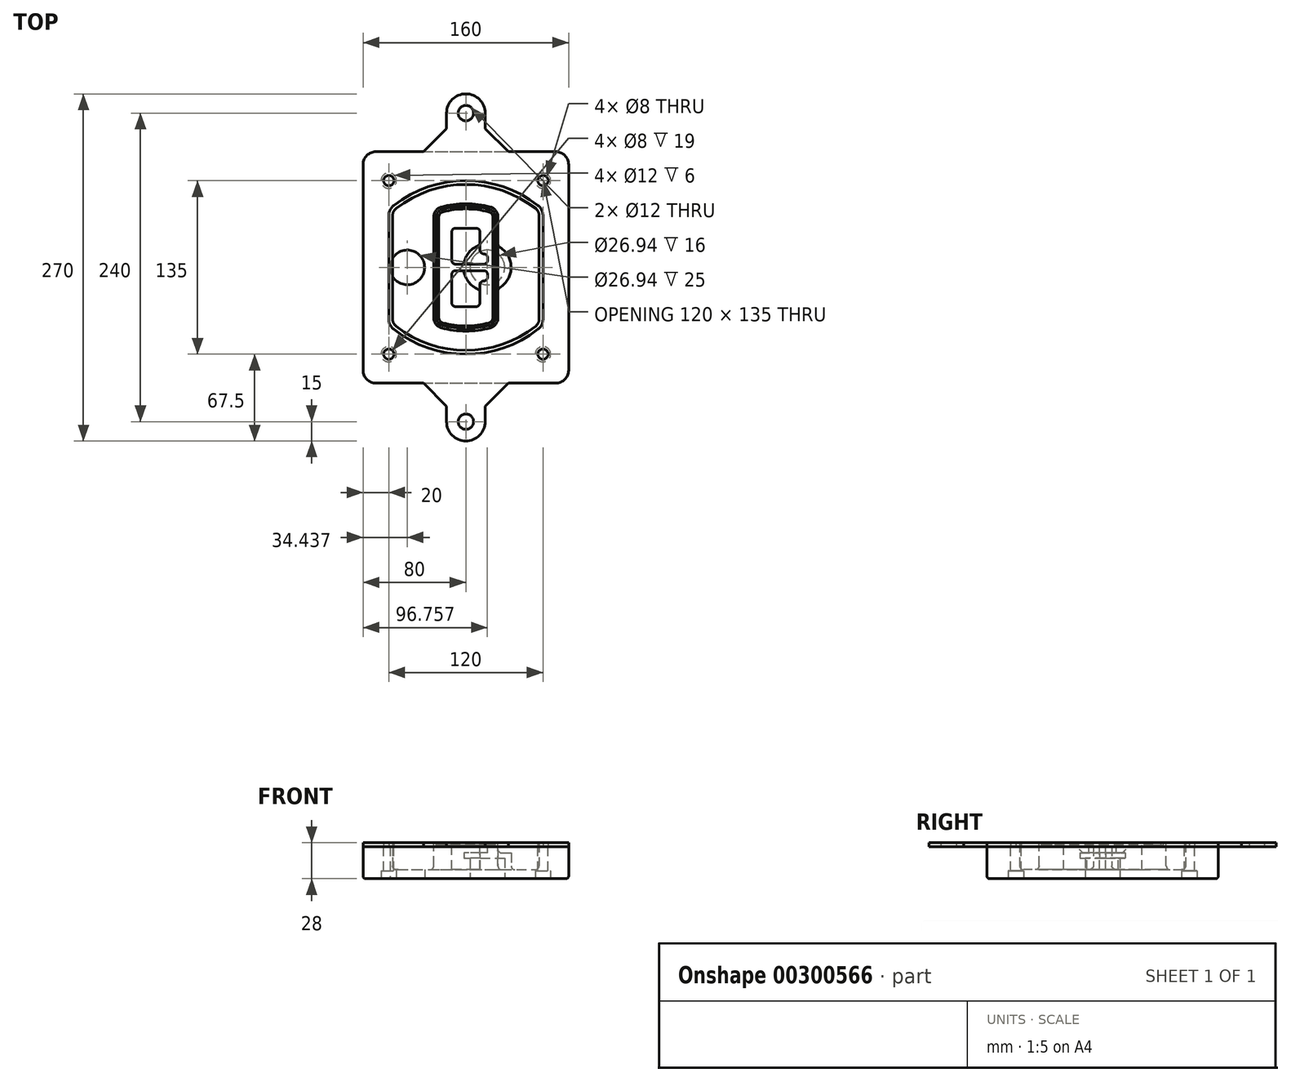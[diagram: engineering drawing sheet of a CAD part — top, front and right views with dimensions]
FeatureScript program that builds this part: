
annotation { "Feature Type Name" : "Feature", "Feature Type Description" : "" }
export const myFeature = defineFeature(function(context is Context, id is Id, definition is map)
    precondition{}
    {
        {
            var Q0;
            Q0=qCreatedBy(makeId("Top.planeOp"),FACE);
            var sketch = newSketch(context, id + "F0", { "sketchPlane" : qUnion([Q0])});
            skPoint(sketch, "E0.rect.middle", {"position": v(0, 0) * mm});
            skLineSegment(sketch, "E1.bottom", {"start": v(-70, -90) * mm, "end": v(70, -90) * mm});
            skLineSegment(sketch, "E1.top", {"start": v(-70, 90) * mm, "end": v(70, 90) * mm});
            skLineSegment(sketch, "E1.left", {"start": v(-80, -80) * mm, "end": v(-80, 80) * mm});
            skLineSegment(sketch, "E1.right", {"start": v(80, -80) * mm, "end": v(80, 80) * mm});
            skLineSegment(sketch, "E2", {"start": v(-80, 90) * mm, "end": v(80, -90) * mm, "construction": true});
            skLineSegment(sketch, "E3", {"start": v(80, 90) * mm, "end": v(-80, -90) * mm, "construction": true});
            skCircle(sketch, "E4", {"center": v(-60, 67.5) * mm, "radius": 4 * mm});
            skCircle(sketch, "E5", {"center": v(60, 67.5) * mm, "radius": 4 * mm});
            skCircle(sketch, "E6", {"center": v(60, -67.5) * mm, "radius": 4 * mm});
            skCircle(sketch, "E7", {"center": v(-60, -67.5) * mm, "radius": 4 * mm});
            skLineSegment(sketch, "E8", {"start": v(-60, 67.5) * mm, "end": v(60, 67.5) * mm, "construction": true});
            skLineSegment(sketch, "E9", {"start": v(60, 67.5) * mm, "end": v(60, -67.5) * mm, "construction": true});
            skLineSegment(sketch, "E10", {"start": v(60, -67.5) * mm, "end": v(-60, -67.5) * mm, "construction": true});
            skLineSegment(sketch, "E11", {"start": v(-60, -67.5) * mm, "end": v(-60, 67.5) * mm, "construction": true});
            skLineSegment(sketch, "E12", {"start": v(-60, 40.3) * mm, "end": v(-60, -40.3) * mm});
            skLineSegment(sketch, "E13", {"start": v(60, 40.3) * mm, "end": v(60, -40.3) * mm});
            skArc(sketch, "E14", {"start": v(56.15, 48.18) * mm, "mid": v(0, 67.5) * mm, "end": v(-56.15, 48.18) * mm});
            skArc(sketch, "E15", {"start": v(-56.15, -48.18) * mm, "mid": v(0, -67.5) * mm, "end": v(56.15, -48.18) * mm});
            skLineSegment(sketch, "E16", {"start": v(-60, 0) * mm, "end": v(60, 0) * mm, "construction": true});
            skPoint(sketch, "E17.visualSharp", {"position": v(-60, -45) * mm});
            skArc(sketch, "E17.filletArc", {"start": v(-60, -40.3) * mm, "mid": v(-58.99, -44.68) * mm, "end": v(-56.15, -48.18) * mm});
            skPoint(sketch, "E18.visualSharp", {"position": v(-60, 45) * mm});
            skArc(sketch, "E18.filletArc", {"start": v(-56.15, 48.18) * mm, "mid": v(-58.99, 44.68) * mm, "end": v(-60, 40.3) * mm});
            skPoint(sketch, "E19.visualSharp", {"position": v(60, 45) * mm});
            skArc(sketch, "E19.filletArc", {"start": v(60, 40.3) * mm, "mid": v(58.99, 44.68) * mm, "end": v(56.15, 48.18) * mm});
            skPoint(sketch, "E20.visualSharp", {"position": v(60, -45) * mm});
            skArc(sketch, "E20.filletArc", {"start": v(56.15, -48.18) * mm, "mid": v(58.99, -44.68) * mm, "end": v(60, -40.3) * mm});
            skPoint(sketch, "E21.visualSharp", {"position": v(-80, 90) * mm});
            skArc(sketch, "E21.filletArc", {"start": v(-70, 90) * mm, "mid": v(-77.07, 87.07) * mm, "end": v(-80, 80) * mm});
            skPoint(sketch, "E22.visualSharp", {"position": v(80, 90) * mm});
            skArc(sketch, "E22.filletArc", {"start": v(80, 80) * mm, "mid": v(77.07, 87.07) * mm, "end": v(70, 90) * mm});
            skPoint(sketch, "E23.visualSharp", {"position": v(80, -90) * mm});
            skArc(sketch, "E23.filletArc", {"start": v(70, -90) * mm, "mid": v(77.07, -87.07) * mm, "end": v(80, -80) * mm});
            skPoint(sketch, "E24.visualSharp", {"position": v(-80, -90) * mm});
            skArc(sketch, "E24.filletArc", {"start": v(-80, -80) * mm, "mid": v(-77.07, -87.07) * mm, "end": v(-70, -90) * mm});
            skArc(sketch, "E25.0", {"start": v(57, 40.3) * mm, "mid": v(56.3, 43.36) * mm, "end": v(54.3, 45.81) * mm});
            skLineSegment(sketch, "E25.1", {"start": v(57, 40.3) * mm, "end": v(57, -40.3) * mm});
            skArc(sketch, "E25.2", {"start": v(54.3, -45.81) * mm, "mid": v(56.3, -43.36) * mm, "end": v(57, -40.3) * mm});
            skArc(sketch, "E25.3", {"start": v(-54.3, -45.81) * mm, "mid": v(0, -64.5) * mm, "end": v(54.3, -45.81) * mm});
            skArc(sketch, "E25.4", {"start": v(-57, -40.3) * mm, "mid": v(-56.3, -43.36) * mm, "end": v(-54.3, -45.81) * mm});
            skArc(sketch, "E25.5", {"start": v(54.3, 45.81) * mm, "mid": v(0, 64.5) * mm, "end": v(-54.3, 45.81) * mm});
            skLineSegment(sketch, "E25.6", {"start": v(-57, 40.3) * mm, "end": v(-57, -40.3) * mm});
            skArc(sketch, "E25.7", {"start": v(-54.3, 45.81) * mm, "mid": v(-56.3, 43.36) * mm, "end": v(-57, 40.3) * mm});
            skArc(sketch, "E26.0", {"start": v(-58.62, 51.33) * mm, "mid": v(-62.58, 46.43) * mm, "end": v(-64, 40.3) * mm});
            skArc(sketch, "E26.1", {"start": v(58.62, 51.33) * mm, "mid": v(0, 71.5) * mm, "end": v(-58.62, 51.33) * mm});
            skArc(sketch, "E26.2", {"start": v(64, 40.3) * mm, "mid": v(62.58, 46.43) * mm, "end": v(58.62, 51.33) * mm});
            skLineSegment(sketch, "E26.3", {"start": v(64, 40.3) * mm, "end": v(64, -40.3) * mm});
            skArc(sketch, "E26.4", {"start": v(58.62, -51.33) * mm, "mid": v(62.58, -46.43) * mm, "end": v(64, -40.3) * mm});
            skLineSegment(sketch, "E26.5", {"start": v(-64, 40.3) * mm, "end": v(-64, -40.3) * mm});
            skArc(sketch, "E26.6", {"start": v(-58.62, -51.33) * mm, "mid": v(0, -71.5) * mm, "end": v(58.62, -51.33) * mm});
            skArc(sketch, "E26.7", {"start": v(-64, -40.3) * mm, "mid": v(-62.58, -46.43) * mm, "end": v(-58.62, -51.33) * mm});
            skSolve(sketch);
        }
        {
            var Q0;
            Q0=makeQuery(id+"F0.imprint","IMPRINT",FACE,{"disambiguationData":[TD([[makeQuery(id+"F0.imprint","IMPRINT",EDGE,{"derivedFrom":sQuery(id+"F0.wireOp",EDGE,"E1.bottom")}),1.0]])]});
            var Q1;
            Q1=makeQuery(id+"F0.imprint","IMPRINT",FACE,{"disambiguationData":[TD([[makeQuery(id+"F0.imprint","IMPRINT",EDGE,{"derivedFrom":sQuery(id+"F0.wireOp",EDGE,"E12")}),1.0]])]});
            var Q2;
            Q2=makeQuery(id+"F0.imprint","IMPRINT",FACE,{"disambiguationData":[TD([[makeQuery(id+"F0.imprint","IMPRINT",EDGE,{"derivedFrom":sQuery(id+"F0.wireOp",EDGE,"E25.0")}),1.0]])]});
            var Q3;
            Q3=makeQuery(id+"F0.imprint","IMPRINT",FACE,{"disambiguationData":[TD([[makeQuery(id+"F0.imprint","IMPRINT",EDGE,{"derivedFrom":sQuery(id+"F0.wireOp",EDGE,"E12")}),-1.0]])]});
            extrude(context, id + "F1", {"entities" : qUnion([Q0, Q1, Q2, Q3]), "oppositeDirection" : true, "depth" : 25 * mm});
        }
        {
            var Q0;
            Q0=makeQuery(id+"F0.imprint","IMPRINT",FACE,{"disambiguationData":[TD([[makeQuery(id+"F0.imprint","IMPRINT",EDGE,{"derivedFrom":sQuery(id+"F0.wireOp",EDGE,"E12")}),1.0]])]});
            extrude(context, id + "F2", {"entities" : qUnion([Q0]), "operationType" : NewBodyOperationType.ADD, "depth" : 3 * mm});
        }
        {
            var Q0;
            Q0=makeQuery(id+"F0.imprint","IMPRINT",FACE,{"disambiguationData":[TD([[makeQuery(id+"F0.imprint","IMPRINT",EDGE,{"derivedFrom":sQuery(id+"F0.wireOp",EDGE,"E25.0")}),1.0]])]});
            extrude(context, id + "F3", {"entities" : qUnion([Q0]), "operationType" : NewBodyOperationType.REMOVE, "oppositeDirection" : true, "depth" : 18 * mm});
        }
        {
            var Q0;
            Q0=makeQuery(id+"F2.opExtrude","CAP_FACE",FACE,{"disambiguationData":[OSD([sQuery(id+"F0.wireOp",EDGE,"E12"),sQuery(id+"F0.wireOp",EDGE,"E13"),sQuery(id+"F0.wireOp",EDGE,"E14"),sQuery(id+"F0.wireOp",EDGE,"E15"),sQuery(id+"F0.wireOp",EDGE,"E17.filletArc"),sQuery(id+"F0.wireOp",EDGE,"E18.filletArc"),sQuery(id+"F0.wireOp",EDGE,"E19.filletArc"),sQuery(id+"F0.wireOp",EDGE,"E20.filletArc"),sQuery(id+"F0.wireOp",EDGE,"E25.0"),sQuery(id+"F0.wireOp",EDGE,"E25.1"),sQuery(id+"F0.wireOp",EDGE,"E25.2"),sQuery(id+"F0.wireOp",EDGE,"E25.3"),sQuery(id+"F0.wireOp",EDGE,"E25.4"),sQuery(id+"F0.wireOp",EDGE,"E25.5"),sQuery(id+"F0.wireOp",EDGE,"E25.6"),sQuery(id+"F0.wireOp",EDGE,"E25.7")])],"isStart":false});
            var sketch = newSketch(context, id + "F4", { "sketchPlane" : qUnion([Q0])});
            skArc(sketch, "E27.0", {"start": v(-19.08, -46.97) * mm, "mid": v(0, -49.5) * mm, "end": v(19.08, -46.97) * mm});
            skArc(sketch, "E28.0", {"start": v(19.08, 46.97) * mm, "mid": v(0, 49.5) * mm, "end": v(-19.08, 46.97) * mm});
            skLineSegment(sketch, "E29", {"start": v(-25, 39.25) * mm, "end": v(-25, -39.25) * mm});
            skLineSegment(sketch, "E30", {"start": v(25, 39.25) * mm, "end": v(25, -39.25) * mm});
            skLineSegment(sketch, "E31", {"start": v(-25, 45.1) * mm, "end": v(25, 45.1) * mm, "construction": true});
            skLineSegment(sketch, "E32", {"start": v(-25, -45.1) * mm, "end": v(25, -45.1) * mm, "construction": true});
            skPoint(sketch, "E33.visualSharp", {"position": v(-25, 45.1) * mm});
            skArc(sketch, "E33.filletArc", {"start": v(-19.08, 46.97) * mm, "mid": v(-23.35, 44.11) * mm, "end": v(-25, 39.25) * mm});
            skPoint(sketch, "E34.visualSharp", {"position": v(25, 45.1) * mm});
            skArc(sketch, "E34.filletArc", {"start": v(25, 39.25) * mm, "mid": v(23.35, 44.11) * mm, "end": v(19.08, 46.97) * mm});
            skPoint(sketch, "E35.visualSharp", {"position": v(25, -45.1) * mm});
            skArc(sketch, "E35.filletArc", {"start": v(19.08, -46.97) * mm, "mid": v(23.35, -44.11) * mm, "end": v(25, -39.25) * mm});
            skPoint(sketch, "E36.visualSharp", {"position": v(-25, -45.1) * mm});
            skArc(sketch, "E36.filletArc", {"start": v(-25, -39.25) * mm, "mid": v(-23.35, -44.11) * mm, "end": v(-19.08, -46.97) * mm});
            skArc(sketch, "E37.0", {"start": v(54.3, 45.81) * mm, "mid": v(0, 64.5) * mm, "end": v(-54.3, 45.81) * mm});
            skArc(sketch, "E37.1", {"start": v(-54.3, 45.81) * mm, "mid": v(-56.3, 43.36) * mm, "end": v(-57, 40.3) * mm});
            skLineSegment(sketch, "E37.2", {"start": v(-57, 40.3) * mm, "end": v(-57, -40.3) * mm});
            skArc(sketch, "E37.3", {"start": v(-57, -40.3) * mm, "mid": v(-56.3, -43.36) * mm, "end": v(-54.3, -45.81) * mm});
            skArc(sketch, "E37.4", {"start": v(-54.3, -45.81) * mm, "mid": v(0, -64.5) * mm, "end": v(54.3, -45.81) * mm});
            skArc(sketch, "E37.5", {"start": v(54.3, -45.81) * mm, "mid": v(56.3, -43.36) * mm, "end": v(57, -40.3) * mm});
            skLineSegment(sketch, "E37.6", {"start": v(57, 40.3) * mm, "end": v(57, -40.3) * mm});
            skArc(sketch, "E37.7", {"start": v(57, 40.3) * mm, "mid": v(56.3, 43.36) * mm, "end": v(54.3, 45.81) * mm});
            skLineSegment(sketch, "E38.0", {"start": v(23, 39.25) * mm, "end": v(23, -39.25) * mm});
            skArc(sketch, "E38.1", {"start": v(18.56, -45.04) * mm, "mid": v(21.76, -42.9) * mm, "end": v(23, -39.25) * mm});
            skArc(sketch, "E38.2", {"start": v(-18.56, -45.04) * mm, "mid": v(0, -47.5) * mm, "end": v(18.56, -45.04) * mm});
            skArc(sketch, "E38.3", {"start": v(-23, -39.25) * mm, "mid": v(-21.76, -42.9) * mm, "end": v(-18.56, -45.04) * mm});
            skLineSegment(sketch, "E38.4", {"start": v(-23, 39.25) * mm, "end": v(-23, -39.25) * mm});
            skArc(sketch, "E38.5", {"start": v(23, 39.25) * mm, "mid": v(21.76, 42.9) * mm, "end": v(18.56, 45.04) * mm});
            skArc(sketch, "E38.6", {"start": v(-18.56, 45.04) * mm, "mid": v(-21.76, 42.9) * mm, "end": v(-23, 39.25) * mm});
            skArc(sketch, "E38.7", {"start": v(18.56, 45.04) * mm, "mid": v(0, 47.5) * mm, "end": v(-18.56, 45.04) * mm});
            skArc(sketch, "E39.0", {"start": v(21, 39.25) * mm, "mid": v(20.18, 41.68) * mm, "end": v(18.04, 43.1) * mm});
            skLineSegment(sketch, "E39.1", {"start": v(21, 39.25) * mm, "end": v(21, -39.25) * mm});
            skArc(sketch, "E39.2", {"start": v(18.04, -43.1) * mm, "mid": v(20.18, -41.68) * mm, "end": v(21, -39.25) * mm});
            skArc(sketch, "E39.3", {"start": v(-18.04, -43.1) * mm, "mid": v(0, -45.5) * mm, "end": v(18.04, -43.1) * mm});
            skArc(sketch, "E39.4", {"start": v(-21, -39.25) * mm, "mid": v(-20.18, -41.68) * mm, "end": v(-18.04, -43.1) * mm});
            skArc(sketch, "E39.5", {"start": v(18.04, 43.1) * mm, "mid": v(0, 45.5) * mm, "end": v(-18.04, 43.1) * mm});
            skLineSegment(sketch, "E39.6", {"start": v(-21, 39.25) * mm, "end": v(-21, -39.25) * mm});
            skArc(sketch, "E39.7", {"start": v(-18.04, 43.1) * mm, "mid": v(-20.18, 41.68) * mm, "end": v(-21, 39.25) * mm});
            skLineSegment(sketch, "E40", {"start": v(-25, 0) * mm, "end": v(25, 0) * mm, "construction": true});
            skLineSegment(sketch, "E41", {"start": v(-11, 5.5) * mm, "end": v(-11, 27.5) * mm});
            skLineSegment(sketch, "E42", {"start": v(-8, 30.5) * mm, "end": v(8, 30.5) * mm});
            skLineSegment(sketch, "E43", {"start": v(11, 27.5) * mm, "end": v(11, 13.5) * mm});
            skLineSegment(sketch, "E44", {"start": v(14, 10.5) * mm, "end": v(14, 10.5) * mm});
            skLineSegment(sketch, "E45", {"start": v(17, 7.5) * mm, "end": v(17, 5.5) * mm});
            skLineSegment(sketch, "E46", {"start": v(14, 2.5) * mm, "end": v(-8, 2.5) * mm});
            skPoint(sketch, "E47.visualSharp", {"position": v(-11, 30.5) * mm});
            skArc(sketch, "E47.filletArc", {"start": v(-8, 30.5) * mm, "mid": v(-10.12, 29.62) * mm, "end": v(-11, 27.5) * mm});
            skPoint(sketch, "E48.visualSharp", {"position": v(11, 30.5) * mm});
            skArc(sketch, "E48.filletArc", {"start": v(11, 27.5) * mm, "mid": v(10.12, 29.62) * mm, "end": v(8, 30.5) * mm});
            skPoint(sketch, "E49.visualSharp", {"position": v(11, 10.5) * mm});
            skArc(sketch, "E49.filletArc", {"start": v(11, 13.5) * mm, "mid": v(11.88, 11.38) * mm, "end": v(14, 10.5) * mm});
            skPoint(sketch, "E50.visualSharp", {"position": v(17, 10.5) * mm});
            skArc(sketch, "E50.filletArc", {"start": v(17, 7.5) * mm, "mid": v(16.12, 9.62) * mm, "end": v(14, 10.5) * mm});
            skPoint(sketch, "E51.visualSharp", {"position": v(17, 2.5) * mm});
            skArc(sketch, "E51.filletArc", {"start": v(14, 2.5) * mm, "mid": v(16.12, 3.38) * mm, "end": v(17, 5.5) * mm});
            skPoint(sketch, "E52.visualSharp", {"position": v(-11, 2.5) * mm});
            skArc(sketch, "E52.filletArc", {"start": v(-11, 5.5) * mm, "mid": v(-10.12, 3.38) * mm, "end": v(-8, 2.5) * mm});
            skLineSegment(sketch, "E53.0.MirrorCS", {"start": v(14, -2.5) * mm, "end": v(-8, -2.5) * mm});
            skArc(sketch, "E54.0.MirrorCS", {"start": v(-11, -5.5) * mm, "mid": v(-10.12, -3.38) * mm, "end": v(-8, -2.5) * mm});
            skLineSegment(sketch, "E55.0.MirrorCS", {"start": v(-11, -5.5) * mm, "end": v(-11, -27.5) * mm});
            skArc(sketch, "E56.0.MirrorCS", {"start": v(-8, -30.5) * mm, "mid": v(-10.12, -29.62) * mm, "end": v(-11, -27.5) * mm});
            skLineSegment(sketch, "E57.0.MirrorCS", {"start": v(-8, -30.5) * mm, "end": v(8, -30.5) * mm});
            skArc(sketch, "E58.0.MirrorCS", {"start": v(11, -27.5) * mm, "mid": v(10.12, -29.62) * mm, "end": v(8, -30.5) * mm});
            skLineSegment(sketch, "E59.0.MirrorCS", {"start": v(11, -27.5) * mm, "end": v(11, -13.5) * mm});
            skArc(sketch, "E60.0.MirrorCS", {"start": v(11, -13.5) * mm, "mid": v(11.88, -11.38) * mm, "end": v(14, -10.5) * mm});
            skArc(sketch, "E61.0.MirrorCS", {"start": v(17, -7.5) * mm, "mid": v(16.12, -9.62) * mm, "end": v(14, -10.5) * mm});
            skLineSegment(sketch, "E62.0.MirrorCS", {"start": v(17, -7.5) * mm, "end": v(17, -5.5) * mm});
            skArc(sketch, "E63.0.MirrorCS", {"start": v(14, -2.5) * mm, "mid": v(16.12, -3.38) * mm, "end": v(17, -5.5) * mm});
            skSolve(sketch);
        }
        {
            var Q0;
            Q0=makeQuery(id+"F4.imprint","IMPRINT",FACE,{"disambiguationData":[TD([[makeQuery(id+"F4.imprint","IMPRINT",EDGE,{"derivedFrom":sQuery(id+"F4.wireOp",EDGE,"E27.0")}),1.0]])]});
            var Q1;
            Q1=makeQuery(id+"F4.imprint","IMPRINT",FACE,{"disambiguationData":[TD([[makeQuery(id+"F4.imprint","IMPRINT",EDGE,{"derivedFrom":sQuery(id+"F4.wireOp",EDGE,"E38.0")}),-1.0]])]});
            var Q2;
            Q2=makeQuery(id+"F4.imprint","IMPRINT",FACE,{"disambiguationData":[TD([[makeQuery(id+"F4.imprint","IMPRINT",EDGE,{"derivedFrom":sQuery(id+"F4.wireOp",EDGE,"E39.0")}),1.0]])]});
            extrude(context, id + "F5", {"entities" : qUnion([Q0, Q1, Q2]), "operationType" : NewBodyOperationType.ADD, "endBound" : BoundingType.UP_TO_NEXT, "oppositeDirection" : true, "depth" : 25 * mm});
        }
        {
            var Q0;
            Q0=makeQuery(id+"F4.imprint","IMPRINT",FACE,{"disambiguationData":[TD([[makeQuery(id+"F4.imprint","IMPRINT",EDGE,{"derivedFrom":sQuery(id+"F4.wireOp",EDGE,"E38.0")}),-1.0]])]});
            extrude(context, id + "F6", {"entities" : qUnion([Q0]), "operationType" : NewBodyOperationType.REMOVE, "oppositeDirection" : true, "depth" : 2 * mm});
        }
        {
            var Q0;
            Q0=makeQuery(id+"F1.opExtrude","CAP_FACE",FACE,{"disambiguationData":[OSD([sQuery(id+"F0.wireOp",EDGE,"E1.bottom"),sQuery(id+"F0.wireOp",EDGE,"E1.top"),sQuery(id+"F0.wireOp",EDGE,"E1.left"),sQuery(id+"F0.wireOp",EDGE,"E1.right"),sQuery(id+"F0.wireOp",EDGE,"E4"),sQuery(id+"F0.wireOp",EDGE,"E5"),sQuery(id+"F0.wireOp",EDGE,"E6"),sQuery(id+"F0.wireOp",EDGE,"E7"),sQuery(id+"F0.wireOp",EDGE,"E21.filletArc"),sQuery(id+"F0.wireOp",EDGE,"E22.filletArc"),sQuery(id+"F0.wireOp",EDGE,"E23.filletArc"),sQuery(id+"F0.wireOp",EDGE,"E24.filletArc")])],"isStart":false});
            var sketch = newSketch(context, id + "F7", { "sketchPlane" : qUnion([Q0])});
            skCircle(sketch, "E64", {"center": v(16.76, 0) * mm, "radius": 13.47 * mm});
            skCircle(sketch, "E65", {"center": v(-45.56, 0) * mm, "radius": 13.47 * mm});
            skLineSegment(sketch, "E66", {"start": v(80, 0) * mm, "end": v(-80, 0) * mm});
            skCircle(sketch, "E67", {"center": v(16.76, 0) * mm, "radius": 18.47 * mm});
            skCircle(sketch, "E68", {"center": v(60, -67.5) * mm, "radius": 6 * mm});
            skCircle(sketch, "E69", {"center": v(-60, -67.5) * mm, "radius": 6 * mm});
            skCircle(sketch, "E70", {"center": v(-60, 67.5) * mm, "radius": 6 * mm});
            skCircle(sketch, "E71", {"center": v(60, 67.5) * mm, "radius": 6 * mm});
            skSolve(sketch);
        }
        {
            var Q0;
            {var subQ1=sQuery(id+"F7.wireOp",EDGE,"E66");var subQ4=sQuery(id+"F7.wireOp",EDGE,"E64");var subQ6=makeQuery(id+"F7.imprint","INTERSECT",VERTEX,{"disambiguationData":[OD(0.0)],"derivedFrom":[subQ4,subQ1]});Q0=makeQuery(id+"F7.imprint","IMPRINT",FACE,{"disambiguationData":[TD([[makeQuery(id+"F7.imprint","IMPRINT",EDGE,{"disambiguationData":[TD([[subQ6,-1.0]])],"derivedFrom":subQ4}),-1.0]])]});}
            var Q1;
            {var subQ0=sQuery(id+"F7.wireOp",EDGE,"E66");var subQ1=sQuery(id+"F7.wireOp",EDGE,"E64");var subQ3=makeQuery(id+"F7.imprint","INTERSECT",VERTEX,{"disambiguationData":[OD(0.0)],"derivedFrom":[subQ1,subQ0]});Q1=makeQuery(id+"F7.imprint","IMPRINT",FACE,{"disambiguationData":[TD([[makeQuery(id+"F7.imprint","IMPRINT",EDGE,{"disambiguationData":[TD([[subQ3,-1.0]])],"derivedFrom":subQ1}),1.0]])]});}
            var Q2;
            {var subQ0=sQuery(id+"F7.wireOp",EDGE,"E66");var subQ1=sQuery(id+"F7.wireOp",EDGE,"E64");var subQ3=makeQuery(id+"F7.imprint","INTERSECT",VERTEX,{"disambiguationData":[OD(0.0)],"derivedFrom":[subQ1,subQ0]});Q2=makeQuery(id+"F7.imprint","IMPRINT",FACE,{"disambiguationData":[TD([[makeQuery(id+"F7.imprint","IMPRINT",EDGE,{"disambiguationData":[TD([[subQ3,1.0]])],"derivedFrom":subQ1}),1.0]])]});}
            var Q3;
            {var subQ1=sQuery(id+"F7.wireOp",EDGE,"E66");var subQ4=sQuery(id+"F7.wireOp",EDGE,"E64");var subQ6=makeQuery(id+"F7.imprint","INTERSECT",VERTEX,{"disambiguationData":[OD(0.0)],"derivedFrom":[subQ4,subQ1]});Q3=makeQuery(id+"F7.imprint","IMPRINT",FACE,{"disambiguationData":[TD([[makeQuery(id+"F7.imprint","IMPRINT",EDGE,{"disambiguationData":[TD([[subQ6,1.0]])],"derivedFrom":subQ4}),-1.0]])]});}
            extrude(context, id + "F8", {"entities" : qUnion([Q0, Q1, Q2, Q3]), "operationType" : NewBodyOperationType.ADD, "oppositeDirection" : true, "depth" : 20 * mm});
        }
        {
            var Q0;
            {var subQ0=sQuery(id+"F7.wireOp",EDGE,"E66");var subQ1=sQuery(id+"F7.wireOp",EDGE,"E64");var subQ3=makeQuery(id+"F7.imprint","INTERSECT",VERTEX,{"disambiguationData":[OD(0.0)],"derivedFrom":[subQ1,subQ0]});Q0=makeQuery(id+"F7.imprint","IMPRINT",FACE,{"disambiguationData":[TD([[makeQuery(id+"F7.imprint","IMPRINT",EDGE,{"disambiguationData":[TD([[subQ3,-1.0]])],"derivedFrom":subQ1}),1.0]])]});}
            var Q1;
            {var subQ0=sQuery(id+"F7.wireOp",EDGE,"E66");var subQ1=sQuery(id+"F7.wireOp",EDGE,"E64");var subQ3=makeQuery(id+"F7.imprint","INTERSECT",VERTEX,{"disambiguationData":[OD(0.0)],"derivedFrom":[subQ1,subQ0]});Q1=makeQuery(id+"F7.imprint","IMPRINT",FACE,{"disambiguationData":[TD([[makeQuery(id+"F7.imprint","IMPRINT",EDGE,{"disambiguationData":[TD([[subQ3,1.0]])],"derivedFrom":subQ1}),1.0]])]});}
            extrude(context, id + "F9", {"entities" : qUnion([Q0, Q1]), "operationType" : NewBodyOperationType.REMOVE, "oppositeDirection" : true, "depth" : 16 * mm});
        }
        {
            var Q0;
            {var subQ0=sQuery(id+"F7.wireOp",EDGE,"E66");var subQ1=sQuery(id+"F7.wireOp",EDGE,"E65");var subQ3=makeQuery(id+"F7.imprint","INTERSECT",VERTEX,{"disambiguationData":[OD(0.0)],"derivedFrom":[subQ1,subQ0]});Q0=makeQuery(id+"F7.imprint","IMPRINT",FACE,{"disambiguationData":[TD([[makeQuery(id+"F7.imprint","IMPRINT",EDGE,{"disambiguationData":[TD([[subQ3,-1.0]])],"derivedFrom":subQ1}),1.0]])]});}
            var Q1;
            {var subQ0=sQuery(id+"F7.wireOp",EDGE,"E66");var subQ1=sQuery(id+"F7.wireOp",EDGE,"E65");var subQ3=makeQuery(id+"F7.imprint","INTERSECT",VERTEX,{"disambiguationData":[OD(0.0)],"derivedFrom":[subQ1,subQ0]});Q1=makeQuery(id+"F7.imprint","IMPRINT",FACE,{"disambiguationData":[TD([[makeQuery(id+"F7.imprint","IMPRINT",EDGE,{"disambiguationData":[TD([[subQ3,1.0]])],"derivedFrom":subQ1}),1.0]])]});}
            extrude(context, id + "F10", {"entities" : qUnion([Q0, Q1]), "operationType" : NewBodyOperationType.REMOVE, "oppositeDirection" : true, "depth" : 25 * mm});
        }
        {
            var Q0;
            Q0=makeQuery(id+"F7.imprint","IMPRINT",FACE,{"disambiguationData":[TD([[makeQuery(id+"F7.imprint","IMPRINT",EDGE,{"derivedFrom":sQuery(id+"F7.wireOp",EDGE,"E68")}),1.0]])]});
            var Q1;
            Q1=makeQuery(id+"F7.imprint","IMPRINT",FACE,{"disambiguationData":[TD([[makeQuery(id+"F7.imprint","IMPRINT",EDGE,{"derivedFrom":makeQuery(id+"F1.opExtrude","CAP_EDGE",EDGE,{"disambiguationData":[OSD([sQuery(id+"F0.wireOp",EDGE,"E5")])],"isStart":false})}),-1.0]])]});
            var Q2;
            Q2=makeQuery(id+"F7.imprint","IMPRINT",FACE,{"disambiguationData":[TD([[makeQuery(id+"F7.imprint","IMPRINT",EDGE,{"derivedFrom":sQuery(id+"F7.wireOp",EDGE,"E69")}),1.0]])]});
            var Q3;
            Q3=makeQuery(id+"F7.imprint","IMPRINT",FACE,{"disambiguationData":[TD([[makeQuery(id+"F7.imprint","IMPRINT",EDGE,{"derivedFrom":makeQuery(id+"F1.opExtrude","CAP_EDGE",EDGE,{"disambiguationData":[OSD([sQuery(id+"F0.wireOp",EDGE,"E4")])],"isStart":false})}),-1.0]])]});
            var Q4;
            Q4=makeQuery(id+"F7.imprint","IMPRINT",FACE,{"disambiguationData":[TD([[makeQuery(id+"F7.imprint","IMPRINT",EDGE,{"derivedFrom":sQuery(id+"F7.wireOp",EDGE,"E70")}),1.0]])]});
            var Q5;
            Q5=makeQuery(id+"F7.imprint","IMPRINT",FACE,{"disambiguationData":[TD([[makeQuery(id+"F7.imprint","IMPRINT",EDGE,{"derivedFrom":makeQuery(id+"F1.opExtrude","CAP_EDGE",EDGE,{"disambiguationData":[OSD([sQuery(id+"F0.wireOp",EDGE,"E7")])],"isStart":false})}),-1.0]])]});
            var Q6;
            Q6=makeQuery(id+"F7.imprint","IMPRINT",FACE,{"disambiguationData":[TD([[makeQuery(id+"F7.imprint","IMPRINT",EDGE,{"derivedFrom":sQuery(id+"F7.wireOp",EDGE,"E71")}),1.0]])]});
            var Q7;
            Q7=makeQuery(id+"F7.imprint","IMPRINT",FACE,{"disambiguationData":[TD([[makeQuery(id+"F7.imprint","IMPRINT",EDGE,{"derivedFrom":makeQuery(id+"F1.opExtrude","CAP_EDGE",EDGE,{"disambiguationData":[OSD([sQuery(id+"F0.wireOp",EDGE,"E6")])],"isStart":false})}),-1.0]])]});
            extrude(context, id + "F11", {"entities" : qUnion([Q0, Q1, Q2, Q3, Q4, Q5, Q6, Q7]), "operationType" : NewBodyOperationType.REMOVE, "oppositeDirection" : true, "depth" : 6 * mm});
        }
        {
            var Q0;
            Q0=makeQuery(id+"F9.boolean.opBoolean","COPY",FACE,{"derivedFrom":makeQuery(id+"F9.opExtrude","CAP_FACE",FACE,{"disambiguationData":[OSD([sQuery(id+"F7.wireOp",EDGE,"E64")])],"isStart":false})});
            var sketch = newSketch(context, id + "F12", { "sketchPlane" : qUnion([Q0])});
            skArc(sketch, "E72.0", {"start": v(11, 17.55) * mm, "mid": v(2.57, 11.82) * mm, "end": v(-1.54, 2.5) * mm});
            skArc(sketch, "E72.1", {"start": v(-1.54, -2.5) * mm, "mid": v(2.57, -11.82) * mm, "end": v(11, -17.55) * mm});
            skLineSegment(sketch, "E73", {"start": v(-1.54, -2.5) * mm, "end": v(14, -2.5) * mm});
            skLineSegment(sketch, "E74.0", {"start": v(14, 2.5) * mm, "end": v(-1.54, 2.5) * mm});
            skArc(sketch, "E74.1", {"start": v(14, 2.5) * mm, "mid": v(16.12, 3.38) * mm, "end": v(17, 5.5) * mm});
            skLineSegment(sketch, "E74.2", {"start": v(17, 7.5) * mm, "end": v(17, 5.5) * mm});
            skArc(sketch, "E74.3", {"start": v(17, 7.5) * mm, "mid": v(16.12, 9.62) * mm, "end": v(14, 10.5) * mm});
            skArc(sketch, "E74.4", {"start": v(11, 13.5) * mm, "mid": v(11.88, 11.38) * mm, "end": v(14, 10.5) * mm});
            skLineSegment(sketch, "E74.5", {"start": v(11, 17.55) * mm, "end": v(11, 13.5) * mm});
            skLineSegment(sketch, "E74.7", {"start": v(14, -2.5) * mm, "end": v(-1.54, -2.5) * mm});
            skArc(sketch, "E74.8", {"start": v(14, -2.5) * mm, "mid": v(16.12, -3.38) * mm, "end": v(17, -5.5) * mm});
            skLineSegment(sketch, "E74.9", {"start": v(17, -7.5) * mm, "end": v(17, -5.5) * mm});
            skArc(sketch, "E74.10", {"start": v(17, -7.5) * mm, "mid": v(16.12, -9.62) * mm, "end": v(14, -10.5) * mm});
            skArc(sketch, "E74.11", {"start": v(11, -13.5) * mm, "mid": v(11.88, -11.38) * mm, "end": v(14, -10.5) * mm});
            skLineSegment(sketch, "E74.12", {"start": v(11, -17.55) * mm, "end": v(11, -13.5) * mm});
            skPoint(sketch, "E75.orphan", {"position": v(11, -27.5) * mm});
            skPoint(sketch, "E76.orphan", {"position": v(-8, -2.5) * mm});
            skPoint(sketch, "E77.orphan", {"position": v(-8, 2.5) * mm});
            skPoint(sketch, "E78.orphan", {"position": v(11, 27.5) * mm});
            skSolve(sketch);
        }
        {
            var Q0;
            {var subQ7=sQuery(id+"F12.wireOp",EDGE,"E72.0");var subQ14=sQuery(id+"F12.wireOp",EDGE,"E72.1");var subQ16=sQuery(id+"F12.wireOp",EDGE,"E74.1");var subQ18=sQuery(id+"F12.wireOp",EDGE,"E74.8");Q0=qUnion([makeQuery(id+"F12.imprint","IMPRINT",FACE,{"disambiguationData":[TD([[makeQuery(id+"F12.imprint","IMPRINT",EDGE,{"derivedFrom":subQ7}),1.0]])]}),makeQuery(id+"F12.imprint","IMPRINT",FACE,{"disambiguationData":[TD([[makeQuery(id+"F12.imprint","IMPRINT",EDGE,{"derivedFrom":subQ14}),1.0]])]}),makeQuery(id+"F12.imprint","IMPRINT",FACE,{"disambiguationData":[TD([[makeQuery(id+"F12.imprint","IMPRINT",EDGE,{"derivedFrom":subQ16}),1.0]])]}),makeQuery(id+"F12.imprint","IMPRINT",FACE,{"disambiguationData":[TD([[makeQuery(id+"F12.imprint","IMPRINT",EDGE,{"derivedFrom":subQ18}),-1.0]])]})]);}
            var Q1;
            Q1=makeQuery(id+"F5.boolean.opBoolean","SPLIT",FACE,{"disambiguationData":[TD([makeQuery(id+"F5.opExtrude","SWEPT_FACE",FACE,{"disambiguationData":[OSD([sQuery(id+"F4.wireOp",EDGE,"E41")])]})])],"derivedFrom":makeQuery(id+"F3.boolean.opBoolean","COPY",FACE,{"derivedFrom":makeQuery(id+"F3.opExtrude","CAP_FACE",FACE,{"disambiguationData":[OSD([sQuery(id+"F0.wireOp",EDGE,"E25.0"),sQuery(id+"F0.wireOp",EDGE,"E25.1"),sQuery(id+"F0.wireOp",EDGE,"E25.2"),sQuery(id+"F0.wireOp",EDGE,"E25.3"),sQuery(id+"F0.wireOp",EDGE,"E25.4"),sQuery(id+"F0.wireOp",EDGE,"E25.5"),sQuery(id+"F0.wireOp",EDGE,"E25.6"),sQuery(id+"F0.wireOp",EDGE,"E25.7")])],"isStart":false})})});
            extrude(context, id + "F13", {"entities" : qUnion([Q0]), "operationType" : NewBodyOperationType.REMOVE, "endBound" : BoundingType.UP_TO_SURFACE, "endBoundEntityFace" : qUnion([Q1]), "depth" : 25 * mm});
        }
        {
            var Q0;
            Q0=makeQuery(id+"F3.boolean.opBoolean","COPY",EDGE,{"derivedFrom":makeQuery(id+"F3.opExtrude","CAP_EDGE",EDGE,{"disambiguationData":[OSD([sQuery(id+"F0.wireOp",EDGE,"E25.6")])],"isStart":false})});
            var Q1;
            Q1=makeQuery(id+"F8.boolean.opBoolean","INTERSECT",EDGE,{"derivedFrom":[makeQuery(id+"F5.opExtrude","SWEPT_FACE",FACE,{"disambiguationData":[OSD([sQuery(id+"F4.wireOp",EDGE,"E30")])]}),makeQuery(id+"F8.opExtrude","CAP_FACE",FACE,{"disambiguationData":[OSD([sQuery(id+"F7.wireOp",EDGE,"E67")])],"isStart":false})]});
            var Q2;
            Q2=makeQuery(id+"F8.boolean.opBoolean","INTERSECT",EDGE,{"disambiguationData":[OD(1.0)],"derivedFrom":[makeQuery(id+"F5.opExtrude","SWEPT_FACE",FACE,{"disambiguationData":[OSD([sQuery(id+"F4.wireOp",EDGE,"E30")])]}),makeQuery(id+"F8.opExtrude","SWEPT_FACE",FACE,{"disambiguationData":[OSD([sQuery(id+"F7.wireOp",EDGE,"E67")])]})]});
            var Q3;
            {var subQ0=sQuery(id+"F4.wireOp",EDGE,"E30");Q3=makeQuery(id+"F8.boolean.opBoolean","SPLIT",EDGE,{"disambiguationData":[TD([makeQuery(id+"F5.opExtrude","SWEPT_FACE",FACE,{"disambiguationData":[OSD([sQuery(id+"F4.wireOp",EDGE,"E35.filletArc")])]})])],"derivedFrom":makeQuery(id+"F5.opExtrude","CAP_EDGE",EDGE,{"disambiguationData":[OSD([subQ0])],"isStart":false})});}
            var Q4;
            {var subQ0=sQuery(id+"F0.wireOp",EDGE,"E25.7");var subQ1=sQuery(id+"F0.wireOp",EDGE,"E25.1");var subQ2=sQuery(id+"F0.wireOp",EDGE,"E25.6");var subQ3=sQuery(id+"F0.wireOp",EDGE,"E25.5");var subQ4=sQuery(id+"F0.wireOp",EDGE,"E25.4");var subQ5=sQuery(id+"F0.wireOp",EDGE,"E25.0");var subQ6=sQuery(id+"F0.wireOp",EDGE,"E25.2");var subQ7=sQuery(id+"F0.wireOp",EDGE,"E25.3");Q4=makeQuery(id+"F8.boolean.opBoolean","INTERSECT",EDGE,{"derivedFrom":[makeQuery(id+"F5.boolean.opBoolean","SPLIT",FACE,{"disambiguationData":[TD([makeQuery(id+"F2.opExtrude","SWEPT_FACE",FACE,{"disambiguationData":[OSD([subQ5])]})])],"derivedFrom":makeQuery(id+"F3.boolean.opBoolean","COPY",FACE,{"derivedFrom":makeQuery(id+"F3.opExtrude","CAP_FACE",FACE,{"disambiguationData":[OSD([subQ5,subQ1,subQ6,subQ7,subQ4,subQ3,subQ2,subQ0])],"isStart":false})})}),makeQuery(id+"F8.opExtrude","SWEPT_FACE",FACE,{"disambiguationData":[OSD([sQuery(id+"F7.wireOp",EDGE,"E67")])]})]});}
            var Q5;
            Q5=makeQuery(id+"F8.boolean.opBoolean","INTERSECT",EDGE,{"disambiguationData":[OD(0.0)],"derivedFrom":[makeQuery(id+"F5.opExtrude","SWEPT_FACE",FACE,{"disambiguationData":[OSD([sQuery(id+"F4.wireOp",EDGE,"E30")])]}),makeQuery(id+"F8.opExtrude","SWEPT_FACE",FACE,{"disambiguationData":[OSD([sQuery(id+"F7.wireOp",EDGE,"E67")])]})]});
            fillet(context, id + "F14", {"entities" : qUnion([Q0, Q1, Q2, Q3, Q4, Q5]), "radius" : 3 * mm, "tangentPropagation" : true, "allowEdgeOverflow" : false});
        }
        {
            var Q0;
            Q0=makeQuery(id+"F1.opExtrude","CAP_EDGE",EDGE,{"disambiguationData":[OSD([sQuery(id+"F0.wireOp",EDGE,"E1.bottom")])],"isStart":false});
            fillet(context, id + "F15", {"entities" : qUnion([Q0]), "radius" : 2 * mm, "tangentPropagation" : true, "allowEdgeOverflow" : false});
        }
        {
            var Q0;
            {var subQ0=sQuery(id+"F0.wireOp",EDGE,"E21.filletArc");var subQ1=sQuery(id+"F0.wireOp",EDGE,"E7");var subQ2=sQuery(id+"F0.wireOp",EDGE,"E6");var subQ3=sQuery(id+"F0.wireOp",EDGE,"E5");var subQ4=sQuery(id+"F0.wireOp",EDGE,"E4");var subQ5=sQuery(id+"F0.wireOp",EDGE,"E22.filletArc");var subQ6=sQuery(id+"F0.wireOp",EDGE,"E1.bottom");var subQ7=sQuery(id+"F0.wireOp",EDGE,"E1.right");var subQ8=sQuery(id+"F0.wireOp",EDGE,"E1.top");var subQ9=sQuery(id+"F0.wireOp",EDGE,"E1.left");var subQ10=sQuery(id+"F0.wireOp",EDGE,"E23.filletArc");var subQ11=sQuery(id+"F0.wireOp",EDGE,"E24.filletArc");Q0=makeQuery(id+"F2.boolean.opBoolean","SPLIT",FACE,{"disambiguationData":[TD([makeQuery(id+"F1.opExtrude","SWEPT_FACE",FACE,{"disambiguationData":[OSD([subQ6])]})])],"derivedFrom":makeQuery(id+"F1.opExtrude","CAP_FACE",FACE,{"disambiguationData":[OSD([subQ6,subQ8,subQ9,subQ7,subQ4,subQ3,subQ2,subQ1,subQ0,subQ5,subQ10,subQ11])],"isStart":true})});}
            var sketch = newSketch(context, id + "F16", { "sketchPlane" : qUnion([Q0])});
            skLineSegment(sketch, "E79", {"start": v(0, 90) * mm, "end": v(0, 120) * mm, "construction": true});
            skCircle(sketch, "E80", {"center": v(0, 120) * mm, "radius": 6 * mm});
            skLineSegment(sketch, "E81", {"start": v(-33, 90) * mm, "end": v(-15, 108) * mm});
            skLineSegment(sketch, "E82", {"start": v(-15, 108) * mm, "end": v(-15, 120) * mm});
            skArc(sketch, "E83", {"start": v(15, 120) * mm, "mid": v(0, 135) * mm, "end": v(-15, 120) * mm});
            skLineSegment(sketch, "E84", {"start": v(15, 120) * mm, "end": v(15, 108) * mm});
            skLineSegment(sketch, "E85", {"start": v(15, 108) * mm, "end": v(33, 90) * mm});
            skLineSegment(sketch, "E86", {"start": v(-80, 0) * mm, "end": v(80, 0) * mm, "construction": true});
            skArc(sketch, "E87.MirrorCS", {"start": v(15, -120) * mm, "mid": v(0, -135) * mm, "end": v(-15, -120) * mm});
            skLineSegment(sketch, "E88.MirrorCS", {"start": v(-15, -108) * mm, "end": v(-15, -120) * mm});
            skLineSegment(sketch, "E89.MirrorCS", {"start": v(15, -108) * mm, "end": v(33, -90) * mm});
            skLineSegment(sketch, "E90.MirrorCS", {"start": v(15, -120) * mm, "end": v(15, -108) * mm});
            skLineSegment(sketch, "E91.MirrorCS", {"start": v(-33, -90) * mm, "end": v(-15, -108) * mm});
            skLineSegment(sketch, "E92.MirrorCS", {"start": v(0, -90) * mm, "end": v(0, -120) * mm});
            skCircle(sketch, "E93.MirrorC", {"center": v(0, -120) * mm, "radius": 6 * mm});
            skSolve(sketch);
        }
        {
            var Q0;
            Q0=makeQuery(id+"F16.imprint","IMPRINT",FACE,{"disambiguationData":[TD([[makeQuery(id+"F16.imprint","IMPRINT",EDGE,{"derivedFrom":sQuery(id+"F16.wireOp",EDGE,"E80")}),-1.0]])]});
            var Q1;
            {var subQ0=sQuery(id+"F16.wireOp",EDGE,"E89.MirrorCS");Q1=makeQuery(id+"F16.imprint","IMPRINT",FACE,{"disambiguationData":[TD([[makeQuery(id+"F16.imprint","IMPRINT",EDGE,{"derivedFrom":subQ0}),1.0]])]});}
            var Q2;
            Q2=makeQuery(id+"F16.imprint","IMPRINT",FACE,{"disambiguationData":[TD([[makeQuery(id+"F16.imprint","IMPRINT",EDGE,{"derivedFrom":makeQuery(id+"F1.opExtrude","CAP_EDGE",EDGE,{"disambiguationData":[OSD([sQuery(id+"F0.wireOp",EDGE,"E1.left")])],"isStart":true})}),-1.0]])]});
            var Q3;
            Q3=makeQuery(id+"F2.opExtrude","CAP_FACE",FACE,{"disambiguationData":[OSD([sQuery(id+"F0.wireOp",EDGE,"E12"),sQuery(id+"F0.wireOp",EDGE,"E13"),sQuery(id+"F0.wireOp",EDGE,"E14"),sQuery(id+"F0.wireOp",EDGE,"E15"),sQuery(id+"F0.wireOp",EDGE,"E17.filletArc"),sQuery(id+"F0.wireOp",EDGE,"E18.filletArc"),sQuery(id+"F0.wireOp",EDGE,"E19.filletArc"),sQuery(id+"F0.wireOp",EDGE,"E20.filletArc"),sQuery(id+"F0.wireOp",EDGE,"E25.0"),sQuery(id+"F0.wireOp",EDGE,"E25.1"),sQuery(id+"F0.wireOp",EDGE,"E25.2"),sQuery(id+"F0.wireOp",EDGE,"E25.3"),sQuery(id+"F0.wireOp",EDGE,"E25.4"),sQuery(id+"F0.wireOp",EDGE,"E25.5"),sQuery(id+"F0.wireOp",EDGE,"E25.6"),sQuery(id+"F0.wireOp",EDGE,"E25.7")])],"isStart":false});
            extrude(context, id + "F17", {"entities" : qUnion([Q0, Q1, Q2]), "endBound" : BoundingType.UP_TO_SURFACE, "endBoundEntityFace" : qUnion([Q3]), "depth" : 25 * mm});
        }
    });
